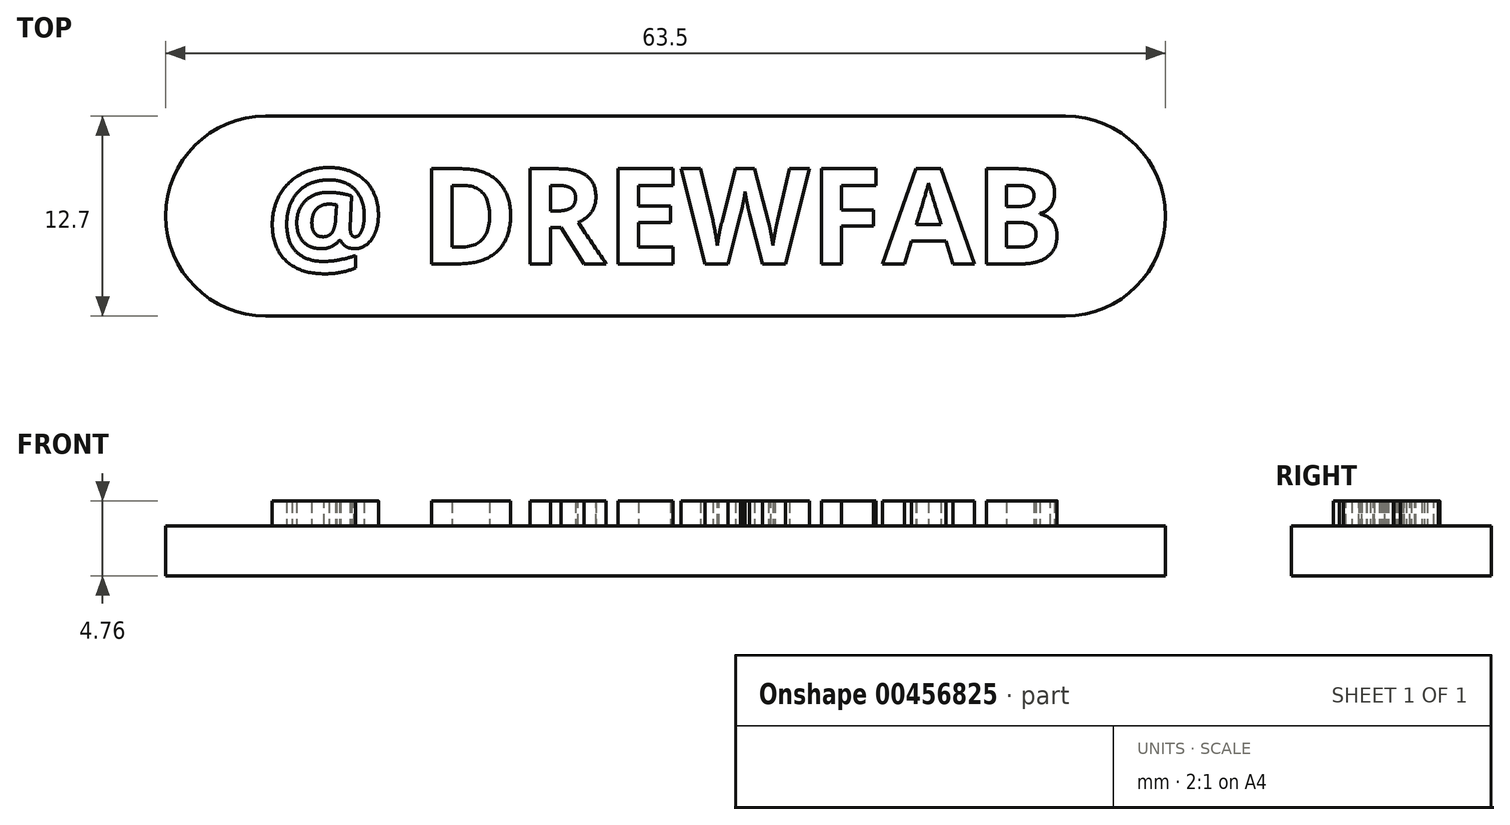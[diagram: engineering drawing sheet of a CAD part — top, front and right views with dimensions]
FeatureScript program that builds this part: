
annotation { "Feature Type Name" : "Feature", "Feature Type Description" : "" }
export const myFeature = defineFeature(function(context is Context, id is Id, definition is map)
    precondition{}
    {
        {
            var Q0;
            Q0=qCreatedBy(makeId("Top.planeOp"),FACE);
            var sketch = newSketch(context, id + "F0", { "sketchPlane" : qUnion([Q0])});
            skLineSegment(sketch, "E0.bottom", {"start": v(25.4, 6.35) * mm, "end": v(-25.4, 6.35) * mm});
            skLineSegment(sketch, "E0.top", {"start": v(25.4, -6.35) * mm, "end": v(-25.4, -6.35) * mm});
            skLineSegment(sketch, "E0.left", {"start": v(25.4, 6.35) * mm, "end": v(25.4, -6.35) * mm, "construction": true});
            skLineSegment(sketch, "E0.right", {"start": v(-25.4, 6.35) * mm, "end": v(-25.4, -6.35) * mm, "construction": true});
            skPoint(sketch, "E0.middle", {"position": v(0, 0) * mm});
            skArc(sketch, "E1", {"start": v(-25.4, 6.35) * mm, "mid": v(-31.75, 0) * mm, "end": v(-25.4, -6.35) * mm});
            skArc(sketch, "E2", {"start": v(25.4, -6.35) * mm, "mid": v(31.75, 0) * mm, "end": v(25.4, 6.35) * mm});
            skSolve(sketch);
        }
        {
            var Q0;
            Q0 = qSketchRegion(id + "F0", true);
            extrude(context, id + "F1", {"entities" : qUnion([Q0]), "depth" : 3.17 * mm});
        }
        {
            var Q0;
            Q0=makeQuery(id+"F1.opExtrude","CAP_FACE",FACE,{"disambiguationData":[OSD([sQuery(id+"F0.wireOp",EDGE,"E0.bottom"),sQuery(id+"F0.wireOp",EDGE,"E0.top"),sQuery(id+"F0.wireOp",EDGE,"E1"),sQuery(id+"F0.wireOp",EDGE,"E2")])],"isStart":false});
            var sketch = newSketch(context, id + "F2", { "sketchPlane" : qUnion([Q0])});
            skText(sketch, "E3", { "text": "@ DREWFAB", "fontName": "OpenSans-Bold.ttf"});
            const initialGuessF2  = {"E3": [-0.0254, -0.00304, 1, 0, 0.00609]};
            skSetInitialGuess(sketch, initialGuessF2);
            skSolve(sketch);
        }
        {
            var Q0;
            Q0 = qSketchRegion(id + "F2", true);
            extrude(context, id + "F3", {"entities" : qUnion([Q0]), "operationType" : NewBodyOperationType.ADD, "depth" : 1.59 * mm});
        }
    });
